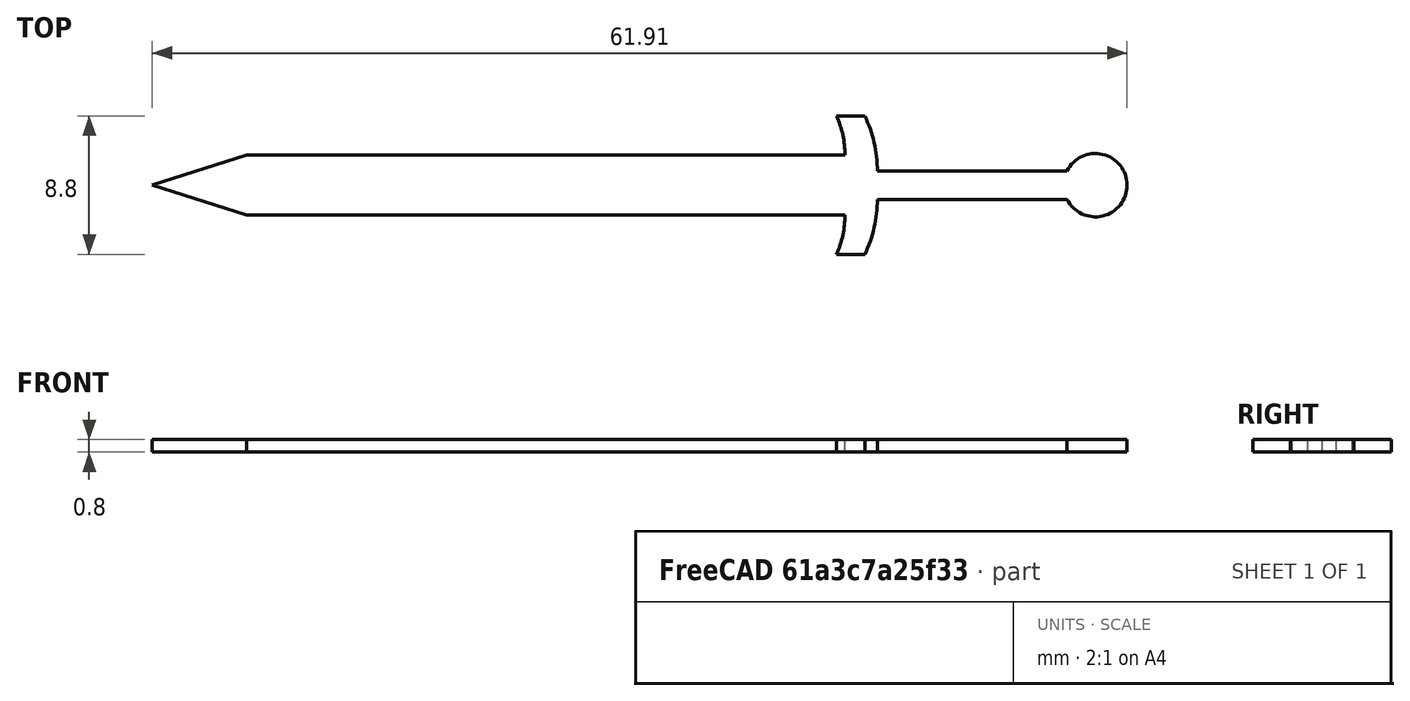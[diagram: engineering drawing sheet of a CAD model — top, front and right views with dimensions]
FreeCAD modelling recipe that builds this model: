
FCSTD DOCUMENT  (FreeCAD 0.21R33771 (Git))
Label: sword
License: All rights reserved
LicenseURL: https://en.wikipedia.org/wiki/All_rights_reserved
objects: Sketcher::SketchObject×1, PartDesign::Pad×1, PartDesign::Body×1, Mesh::Feature×1
note: 4 computed .brp shape members not serialized (recipe doc carries the construction recipe); baked Part::Feature solids carry a one-line shape summary decoded from their .brp

FEATURE [Sketcher::SketchObject] Sketch
  FullyConstrained = true
  MapMode = 5
  Support = -> [XY_Plane]
  sketch-geometry (23):
    g0: LineSegment StartX=-38 StartY=1.9 StartZ=0 EndX=0 EndY=1.9 EndZ=0
    g1: LineSegment StartX=-38 StartY=-1.9 StartZ=0 EndX=0 EndY=-1.9 EndZ=0
    g2: LineSegment StartX=-38 StartY=-1.9 StartZ=0 EndX=-44 EndY=2e-16 EndZ=0
    g3: LineSegment StartX=-38 StartY=1.9 StartZ=0 EndX=-44 EndY=2e-16 EndZ=0
    g4: LineSegment StartX=2.05454 StartY=0.9 StartZ=0 EndX=14.1 EndY=0.9 EndZ=0
    g5: LineSegment StartX=2.05454 StartY=-0.9 StartZ=0 EndX=14.1 EndY=-0.9 EndZ=0
    g6: LineSegment StartX=-38 StartY=1.9 StartZ=0 EndX=-38 EndY=0 EndZ=0
    g7: LineSegment StartX=-38 StartY=-1.9 StartZ=0 EndX=-38 EndY=0 EndZ=0
    g8: ArcOfCircle CenterX=15.9 CenterY=0 CenterZ=0 NormalX=0 NormalY=0 NormalZ=1 AngleXU=0 Radius=2.01246 StartAngle=3.60524 EndAngle=8.96113
    g9: ArcOfCircle CenterX=-6 CenterY=1.9 CenterZ=0 NormalX=0 NormalY=0 NormalZ=1 AngleXU=0 Radius=6 StartAngle=0 EndAngle=0.429775
    g10: ArcOfCircle CenterX=-6 CenterY=-1.9 CenterZ=0 NormalX=0 NormalY=0 NormalZ=1 AngleXU=0 Radius=6 StartAngle=5.85341 EndAngle=6.28319
    g11: ArcOfCircle CenterX=-6 CenterY=-0.899999 CenterZ=0 NormalX=0 NormalY=0 NormalZ=1 AngleXU=0 Radius=8.05455 StartAngle=5.83366 EndAngle=6.28319
    g12: ArcOfCircle CenterX=-6 CenterY=0.9 CenterZ=0 NormalX=0 NormalY=0 NormalZ=1 AngleXU=0 Radius=8.05454 StartAngle=2.2536e-08 EndAngle=0.449525
    g13: LineSegment StartX=-0.545644 StartY=4.4 StartZ=0 EndX=1.25436 EndY=4.4 EndZ=0
    g14: LineSegment StartX=-0.545644 StartY=-4.4 StartZ=0 EndX=1.25436 EndY=-4.4 EndZ=0
    g15: LineSegment StartX=-44 StartY=2e-16 StartZ=0 EndX=15.9 EndY=0 EndZ=0
    g16: LineSegment StartX=-6 StartY=1.9 StartZ=0 EndX=-6 EndY=-1.9 EndZ=0
    g17: LineSegment StartX=0 StartY=1.9 StartZ=0 EndX=0 EndY=-1.9 EndZ=0
    g18: LineSegment StartX=2.05454 StartY=0.9 StartZ=0 EndX=2.05454 EndY=0 EndZ=0
    g19: LineSegment StartX=2.05454 StartY=0 StartZ=0 EndX=2.05454 EndY=-0.9 EndZ=0
    g20: LineSegment StartX=-0.545644 StartY=4.4 StartZ=0 EndX=-0.545644 EndY=0 EndZ=0
    g21: LineSegment StartX=-0.545644 StartY=-4.4 StartZ=0 EndX=-0.545644 EndY=0 EndZ=0
    g22: LineSegment StartX=14.1 StartY=0.9 StartZ=0 EndX=14.1 EndY=-0.9 EndZ=0
  constraints (67):
    c: Coincident(g3,g2)
    c: PointOnObject(g2,g-1)
    c: Coincident(g3,g0)
    c: Coincident(g2,g1)
    c: Coincident(g6,g0)
    c: Coincident(g7,g1)
    c: Coincident(g7,g6)
    c: PointOnObject(g6,g-1)
    c: Vertical(g7)
    c: Vertical(g6)
    c: Horizontal(g0)
    c: Horizontal(g1)
    c: Equal(g7,g6)
    c: PointOnObject(g8,g-1)
    c: Coincident(g15,g2)
    c: Coincident(g15,g8)
    c: Coincident(g4,g8)
    c: Coincident(g5,g8)
    c: Horizontal(g4)
    c: Coincident(g9,g0)
    c: Coincident(g10,g1)
    c: PointOnObject(g10,g1)
    c: PointOnObject(g9,g0)
    c: Coincident(g16,g9)
    c: Coincident(g16,g10)
    c: Vertical(g16)
    c: Coincident(g0,g17)
    c: Coincident(g17,g1)
    c: Vertical(g17)
    c: Coincident(g13,g9)
    c: Coincident(g14,g10)
    c: Horizontal(g14)
    c: Horizontal(g13)
    c: Coincident(g11,g14)
    c: Coincident(g12,g13)
    c: Coincident(g11,g5)
    c: Coincident(g12,g4)
    c: Coincident(g18,g4)
    c: Coincident(g19,g5)
    c: Coincident(g19,g18)
    c: PointOnObject(g18,g15)
    c: Vertical(g19)
    c: Vertical(g18)
    c: Equal(g19,g18)
    c: Coincident(g20,g9)
    c: Coincident(g21,g10)
    c: PointOnObject(g21,g15)
    c: Coincident(g20,g21)
    c: Vertical(g20)
    c: Vertical(g21)
    c: Equal(g14,g13)
    c: Coincident(g22,g4)
    c: Coincident(g22,g5)
    c: PointOnObject(g-1,g17)
    c: DistanceX(g2,g1) = 6
    c: DistanceY(g1,g0) = 3.8
    c: DistanceX(g6,g-1) = 38
    c: DistanceY(g10,g9) = 8.8
    c: DistanceX(g13,g13) = 1.8
    c: DistanceX(g9,g0) = 6
    c: DistanceX(g4,g8) = 1.8
    c: DistanceX(g-1,g8) = 15.9
    c: DistanceY(g5,g4) = 1.8
    c: Horizontal(g5)
    c: Tangent(g18,g12)
    c: Tangent(g19,g11)
    c: PointOnObject(g12,g16)
FEATURE [PartDesign::Pad] Pad
  Direction = (0,0,1)
  Length = 0.8
  Length2 = 10
  Profile = -> Sketch
  ReferenceAxis = -> Sketch [N_Axis]
  Type = 0
FEATURE [PartDesign::Body] Body
  Group = -> [Sketch,Pad]
  Origin = -> Origin
  Tip = -> Pad
FEATURE [Mesh::Feature] Mesh  label="SwordInsert"
